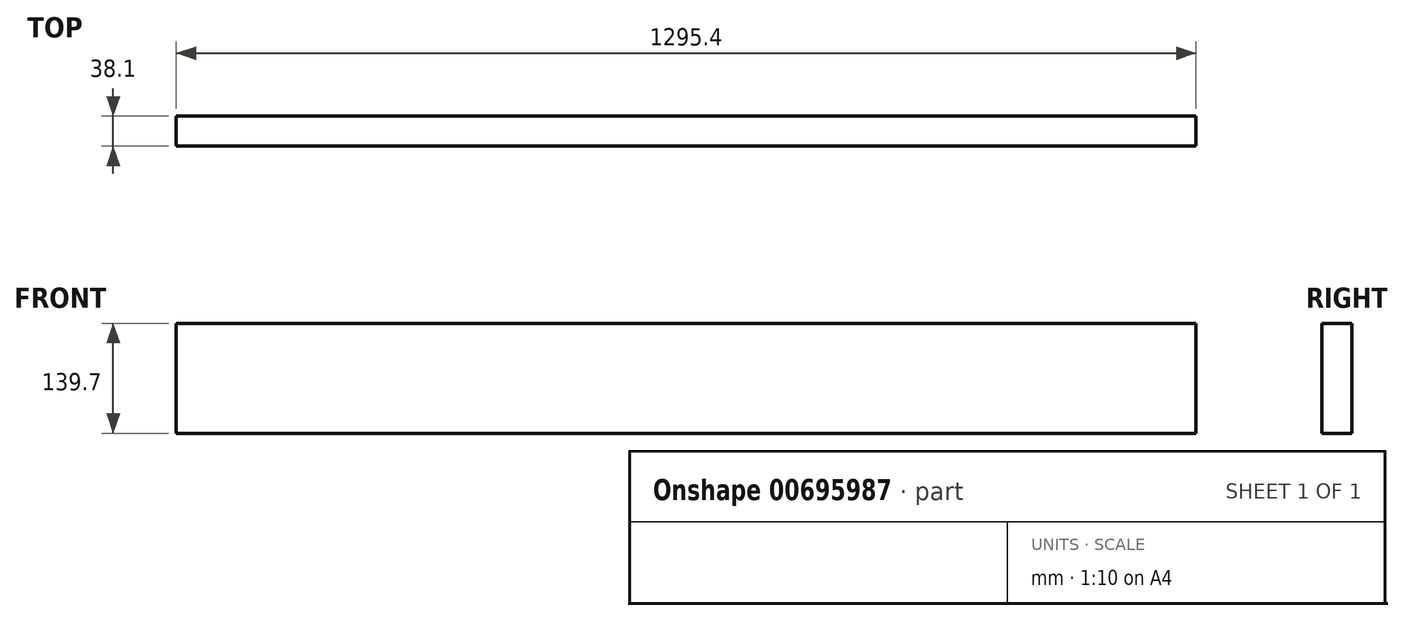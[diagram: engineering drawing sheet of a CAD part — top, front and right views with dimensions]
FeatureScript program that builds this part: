
annotation { "Feature Type Name" : "Feature", "Feature Type Description" : "" }
export const myFeature = defineFeature(function(context is Context, id is Id, definition is map)
    precondition{}
    {
        {
            var Q0;
            Q0=qCreatedBy(makeId("Front.planeOp"),FACE);
            var sketch = newSketch(context, id + "F0", { "sketchPlane" : qUnion([Q0])});
            skLineSegment(sketch, "E0.bottom", {"start": v(0, 0) * mm, "end": v(1295.4, 0) * mm});
            skLineSegment(sketch, "E0.top", {"start": v(0, 139.7) * mm, "end": v(1295.4, 139.7) * mm});
            skLineSegment(sketch, "E0.left", {"start": v(0, 0) * mm, "end": v(0, 139.7) * mm});
            skLineSegment(sketch, "E0.right", {"start": v(1295.4, 0) * mm, "end": v(1295.4, 139.7) * mm});
            skSolve(sketch);
        }
        {
            var Q0;
            Q0 = qSketchRegion(id + "F0", true);
            extrude(context, id + "F1", {"entities" : qUnion([Q0]), "depth" : 38.1 * mm, "offsetDistance" : 25.4 * mm});
        }
    });
